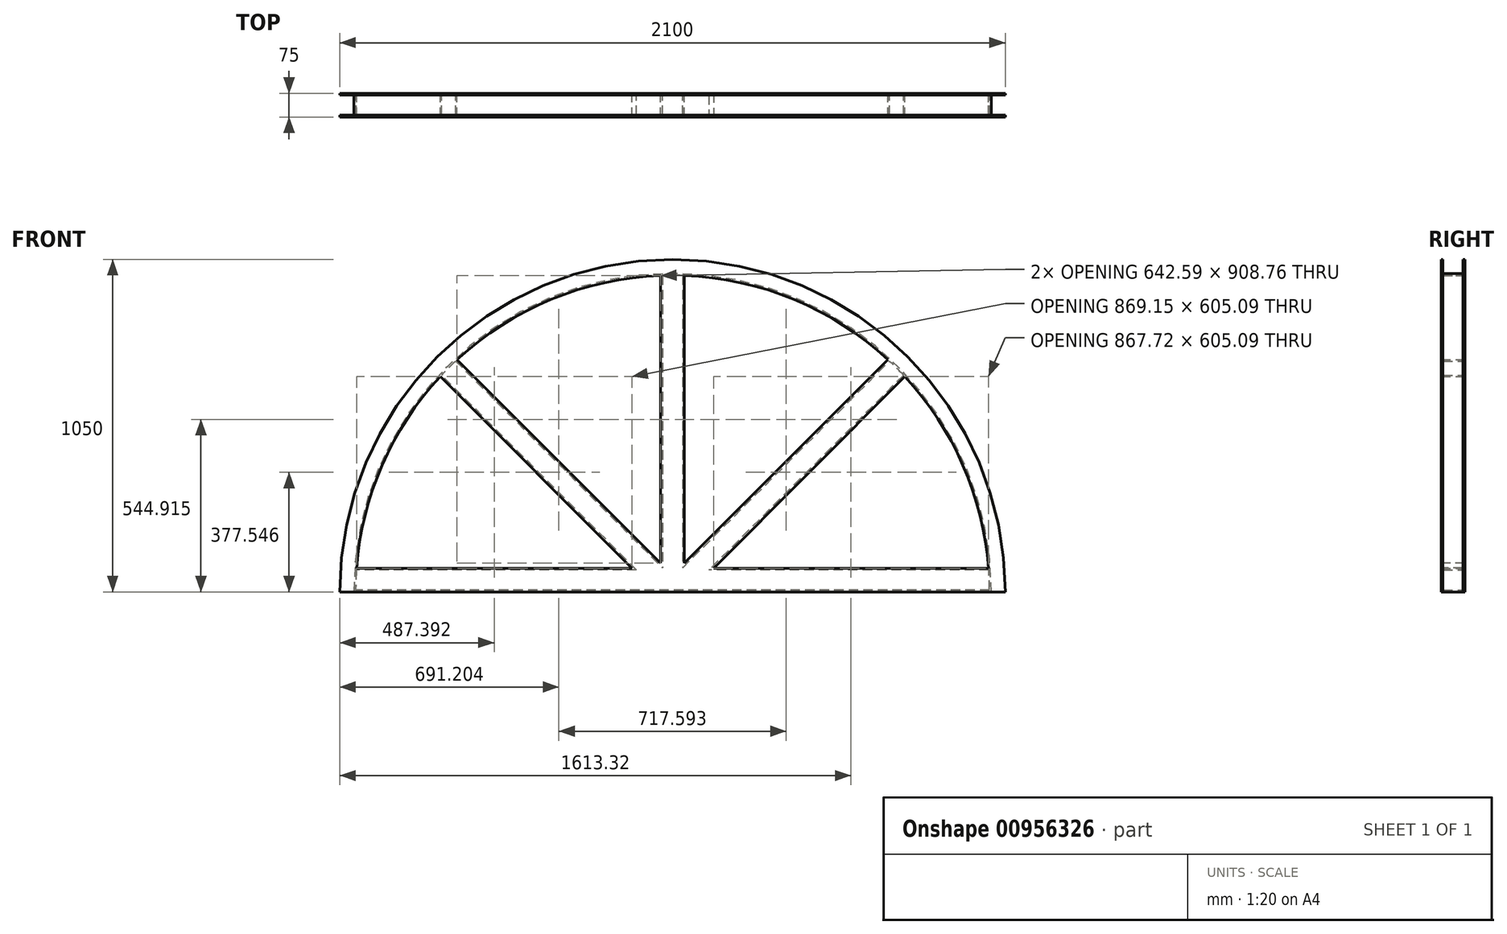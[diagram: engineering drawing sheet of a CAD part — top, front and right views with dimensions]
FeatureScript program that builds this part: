
annotation { "Feature Type Name" : "Feature", "Feature Type Description" : "" }
export const myFeature = defineFeature(function(context is Context, id is Id, definition is map)
    precondition{}
    {
        {
            var Q0;
            Q0=qCreatedBy(makeId("Front.planeOp"),FACE);
            var sketch = newSketch(context, id + "F0", { "sketchPlane" : qUnion([Q0])});
            skArc(sketch, "E0", {"start": v(1000, 0) * mm, "mid": v(0, 1000) * mm, "end": v(-1000, 0) * mm});
            skLineSegment(sketch, "E1", {"start": v(-1000, 0) * mm, "end": v(1000, 0) * mm});
            skLineSegment(sketch, "E2", {"start": v(0, 0) * mm, "end": v(707.1, 707.1) * mm});
            skLineSegment(sketch, "E3", {"start": v(0, 0) * mm, "end": v(-707.1, 707.1) * mm});
            skLineSegment(sketch, "E4", {"start": v(0, 0) * mm, "end": v(0, 1000) * mm});
            skLineSegment(sketch, "E5", {"start": v(-1000, 0) * mm, "end": v(-1050, 0) * mm});
            skLineSegment(sketch, "E6", {"start": v(1000, 0) * mm, "end": v(1050, 0) * mm});
            skArc(sketch, "E7", {"start": v(1050, 0) * mm, "mid": v(0, 1050) * mm, "end": v(-1050, 0) * mm});
            skSolve(sketch);
        }
        {
            var Q0;
            {var subQ0=sQuery(id+"F0.wireOp",EDGE,"E5");Q0=makeQuery(id+"F0.imprint","IMPRINT",FACE,{"disambiguationData":[TD([[makeQuery(id+"F0.imprint","IMPRINT",EDGE,{"derivedFrom":subQ0}),-1.0]])]});}
            extrude(context, id + "F1", {"entities" : qUnion([Q0]), "depth" : 75 * mm, "offsetDistance" : 25 * mm});
        }
        {
            var Q0;
            Q0=makeQuery(id+"F1.opExtrude","SWEPT_FACE",FACE,{"disambiguationData":[OSD([sQuery(id+"F0.wireOp",EDGE,"E7")])]});
            var Q1;
            Q1=makeQuery(id+"F1.opExtrude","SWEPT_FACE",FACE,{"disambiguationData":[OSD([sQuery(id+"F0.wireOp",EDGE,"E6")])]});
            var Q2;
            Q2=makeQuery(id+"F1.opExtrude","SWEPT_FACE",FACE,{"disambiguationData":[OSD([sQuery(id+"F0.wireOp",EDGE,"E5")])]});
            shell(context, id + "F2", {"entities" : qUnion([Q0, Q1, Q2]), "thickness" : 6 * mm});
        }
        {
            var Q0;
            Q0=qCreatedBy(makeId("Right.planeOp"),FACE);
            var sketch = newSketch(context, id + "F3", { "sketchPlane" : qUnion([Q0])});
            skLineSegment(sketch, "E8.bottom", {"start": v(0, 0) * mm, "end": v(-75, 0) * mm});
            skLineSegment(sketch, "E8.top", {"start": v(0, 75) * mm, "end": v(-75, 75) * mm});
            skLineSegment(sketch, "E8.left", {"start": v(0, 0) * mm, "end": v(0, 75) * mm});
            skLineSegment(sketch, "E8.right", {"start": v(-75, 0) * mm, "end": v(-75, 75) * mm});
            skSolve(sketch);
        }
        {
            var Q0;
            Q0 = qSketchRegion(id + "F3", true);
            extrude(context, id + "F4", {"entities" : qUnion([Q0]), "operationType" : NewBodyOperationType.ADD, "depth" : 1000 * mm, "offsetDistance" : 25 * mm});
        }
        {
            var Q0;
            Q0=makeQuery(id+"F1.opExtrude","SWEPT_BODY",BODY,{"disambiguationData":[OSD([sQuery(id+"F0.wireOp",EDGE,"E0"),sQuery(id+"F0.wireOp",EDGE,"E5"),sQuery(id+"F0.wireOp",EDGE,"E6"),sQuery(id+"F0.wireOp",EDGE,"E7")])]});
            var Q1;
            Q1=qCreatedBy(makeId("Right.planeOp"),FACE);
            mirror(context, id + "F5", {"operationType" : NewBodyOperationType.ADD, "entities" : qUnion([Q0]), "mirrorPlane" : qUnion([Q1])});
        }
        {
            var Q0;
            {var subQ0=makeQuery(id+"F4.boolean.opBoolean","MERGE",FACE,{"derivedFrom":[makeQuery(id+"F1.opExtrude","SWEPT_FACE",FACE,{"disambiguationData":[OSD([sQuery(id+"F0.wireOp",EDGE,"E6")])]}),makeQuery(id+"F4.opExtrude","SWEPT_FACE",FACE,{"disambiguationData":[OSD([sQuery(id+"F3.wireOp",EDGE,"E8.bottom")])]})]});Q0=makeQuery(id+"F5.boolean.opBoolean","MERGE",FACE,{"derivedFrom":[makeQuery(id+"F1.opExtrude","SWEPT_FACE",FACE,{"disambiguationData":[OSD([sQuery(id+"F0.wireOp",EDGE,"E5")])]}),subQ0,makeQuery(id+"F5.opPattern","COPY",FACE,{"derivedFrom":subQ0,"instanceName":"1"})]});}
            var sketch = newSketch(context, id + "F6", { "sketchPlane" : qUnion([Q0])});
            skLineSegment(sketch, "E9.bottom", {"start": v(-37.5, 0) * mm, "end": v(37.5, 0) * mm});
            skLineSegment(sketch, "E9.top", {"start": v(-37.5, 75) * mm, "end": v(37.5, 75) * mm});
            skLineSegment(sketch, "E9.left", {"start": v(-37.5, 0) * mm, "end": v(-37.5, 75) * mm});
            skLineSegment(sketch, "E9.right", {"start": v(37.5, 0) * mm, "end": v(37.5, 75) * mm});
            skSolve(sketch);
        }
        {
            var Q0;
            Q0 = qSketchRegion(id + "F6", true);
            extrude(context, id + "F7", {"entities" : qUnion([Q0]), "operationType" : NewBodyOperationType.ADD, "oppositeDirection" : true, "depth" : 1000 * mm, "offsetDistance" : 25 * mm});
        }
        {
            var Q0;
            {var subQ3=sQuery(id+"F0.wireOp",EDGE,"E2");Q0=makeQuery(id+"F0.imprint","IMPRINT",FACE,{"disambiguationData":[TD([[makeQuery(id+"F0.imprint","IMPRINT",EDGE,{"derivedFrom":subQ3}),-1.0]])]});}
            var sketch = newSketch(context, id + "F8", { "sketchPlane" : qUnion([Q0])});
            skArc(sketch, "E10", {"start": v(733.13, 680.1) * mm, "mid": v(707.11, 707.11) * mm, "end": v(680.1, 733.13) * mm});
            skLineSegment(sketch, "E11", {"start": v(733.13, 680.1) * mm, "end": v(84.9, 30.33) * mm});
            skLineSegment(sketch, "E12", {"start": v(84.9, 30.33) * mm, "end": v(-27.01, 30.33) * mm});
            skLineSegment(sketch, "E13", {"start": v(-27.01, 26.02) * mm, "end": v(-27.01, 30.33) * mm});
            skLineSegment(sketch, "E14", {"start": v(-27.01, 26.02) * mm, "end": v(680.1, 733.13) * mm});
            skSolve(sketch);
        }
        {
            var Q0;
            Q0 = qSketchRegion(id + "F8", true);
            extrude(context, id + "F9", {"entities" : qUnion([Q0]), "operationType" : NewBodyOperationType.ADD, "depth" : 75 * mm, "offsetDistance" : 25 * mm});
        }
        {
            var Q0;
            Q0=qCreatedBy(makeId("Front.planeOp"),FACE);
            var sketch = newSketch(context, id + "F10", { "sketchPlane" : qUnion([Q0])});
            skLineSegment(sketch, "E15", {"start": v(-27.48, 44.2) * mm, "end": v(-97.23, 44.2) * mm});
            skLineSegment(sketch, "E16", {"start": v(-97.23, 44.2) * mm, "end": v(-733.62, 680.6) * mm});
            skLineSegment(sketch, "E17", {"start": v(-733.62, 680.6) * mm, "end": v(-680.6, 733.62) * mm});
            skLineSegment(sketch, "E18", {"start": v(-680.6, 733.62) * mm, "end": v(-30.05, 83.09) * mm});
            skLineSegment(sketch, "E19", {"start": v(-30.05, 83.09) * mm, "end": v(-27.48, 44.2) * mm});
            skSolve(sketch);
        }
        {
            var Q0;
            Q0 = qSketchRegion(id + "F10", true);
            extrude(context, id + "F11", {"entities" : qUnion([Q0]), "operationType" : NewBodyOperationType.ADD, "depth" : 75 * mm, "offsetDistance" : 25 * mm});
        }
        {
            var Q0;
            {var subQ0=makeQuery(id+"F4.boolean.opBoolean","MERGE",FACE,{"derivedFrom":[makeQuery(id+"F1.opExtrude","CAP_FACE",FACE,{"disambiguationData":[OSD([sQuery(id+"F0.wireOp",EDGE,"E0"),sQuery(id+"F0.wireOp",EDGE,"E5"),sQuery(id+"F0.wireOp",EDGE,"E6"),sQuery(id+"F0.wireOp",EDGE,"E7")])],"isStart":false}),makeQuery(id+"F4.opExtrude","SWEPT_FACE",FACE,{"disambiguationData":[OSD([sQuery(id+"F3.wireOp",EDGE,"E8.right")])]})]});Q0=makeQuery(id+"F11.boolean.opBoolean","MERGE",FACE,{"derivedFrom":[makeQuery(id+"F9.boolean.opBoolean","MERGE",FACE,{"derivedFrom":[makeQuery(id+"F7.boolean.opBoolean","MERGE",FACE,{"derivedFrom":[makeQuery(id+"F5.boolean.opBoolean","MERGE",FACE,{"derivedFrom":[subQ0,makeQuery(id+"F5.opPattern","COPY",FACE,{"derivedFrom":subQ0,"instanceName":"1"})]}),makeQuery(id+"F7.opExtrude","SWEPT_FACE",FACE,{"disambiguationData":[OSD([sQuery(id+"F6.wireOp",EDGE,"E9.top")])]})]}),makeQuery(id+"F9.opExtrude","CAP_FACE",FACE,{"disambiguationData":[OSD([sQuery(id+"F8.wireOp",EDGE,"E10"),sQuery(id+"F8.wireOp",EDGE,"E11"),sQuery(id+"F8.wireOp",EDGE,"E12"),sQuery(id+"F8.wireOp",EDGE,"E14")])],"isStart":false})]}),makeQuery(id+"F11.opExtrude","CAP_FACE",FACE,{"disambiguationData":[OSD([sQuery(id+"F10.wireOp",EDGE,"E15"),sQuery(id+"F10.wireOp",EDGE,"E16"),sQuery(id+"F10.wireOp",EDGE,"E17"),sQuery(id+"F10.wireOp",EDGE,"E18"),sQuery(id+"F10.wireOp",EDGE,"E19")])],"isStart":false})]});}
            var Q1;
            Q1=makeQuery(id+"F1.opExtrude","SWEPT_BODY",BODY,{"disambiguationData":[OSD([sQuery(id+"F0.wireOp",EDGE,"E0"),sQuery(id+"F0.wireOp",EDGE,"E5"),sQuery(id+"F0.wireOp",EDGE,"E6"),sQuery(id+"F0.wireOp",EDGE,"E7")])]});
            shell(context, id + "F12", {"isHollow" : true, "entities" : qUnion([Q0]), "parts" : qUnion([Q1]), "thickness" : 6 * mm});
        }
    });
